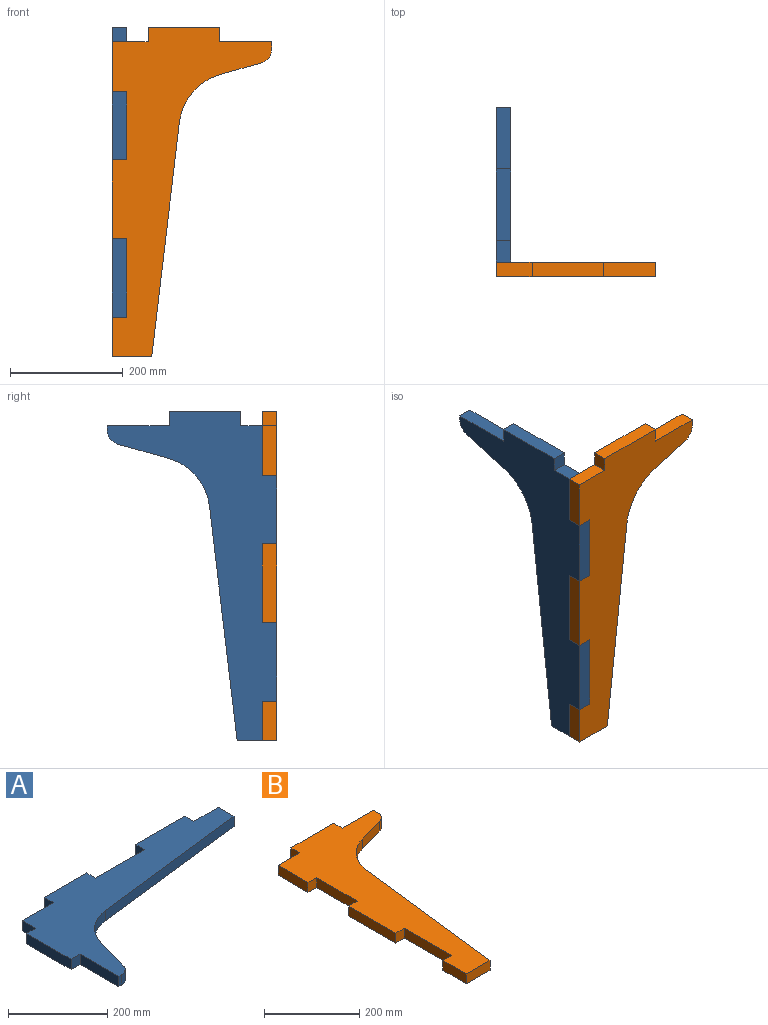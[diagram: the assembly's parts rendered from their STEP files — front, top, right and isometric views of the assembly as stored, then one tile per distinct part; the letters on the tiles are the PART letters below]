
ASSEMBLY  parts=2 mates=1
PART A: 22 faces, bbox 584.2x300.4x25.4 mm
  f0: plane 109.86x25.4mm, normal (-1,0,0), area 2790.5mm2, adj f1,f19,f20,f21
  f1: plane 25.4x8.24mm, normal (0,-1,0), area 209.4mm2, adj f0,f2,f20,f21
  f2: cylinder r=25.4mm len=25.4mm, axis (0,0,-1), area 836.7mm2, adj f1,f3,f20,f21
  f3: plane 89.39x25.4mm, normal (0.96,-0.27,0), area 2358.3mm2, adj f2,f4,f20,f21
  f4: cylinder r=101.6mm len=85.9mm, axis (0,0,-1), area 3043.6mm2, adj f3,f5,f20,f21
  f5: plane 415.09x48.99mm, normal (0.12,-0.99,0), area 10616.3mm2, adj f4,f6,f20,f21
  f6: plane 44.65x25.4mm, normal (1,0,0), area 1134mm2, adj f5,f7,f20,f21
  f7: plane 69.85x25.4mm, normal (0,1,0), area 1774.2mm2, adj f6,f8,f20,f21
  f8: plane 25.4x25.4mm, normal (1,0,0), area 645.2mm2, adj f7,f9,f20,f21
  f9: plane 139.7x25.4mm, normal (0,1,0), area 3548.4mm2, adj f8,f10,f20,f21
  f10: plane 25.4x25.4mm, normal (-1,0,0), area 645.2mm2, adj f9,f11,f20,f21
  f11: plane 139.7x25.4mm, normal (0,1,0), area 3548.4mm2, adj f10,f12,f20,f21
  f12: plane 25.4x25.4mm, normal (1,0,0), area 645.2mm2, adj f11,f13,f20,f21
  f13: plane 120.65x25.4mm, normal (0,1,0), area 3064.5mm2, adj f12,f14,f20,f21
  f14: plane 25.4x25.4mm, normal (-1,0,0), area 645.2mm2, adj f13,f15,f20,f21
  f15: plane 88.9x25.4mm, normal (0,1,0), area 2258.1mm2, adj f14,f16,f20,f21
  f16: plane 38.1x25.4mm, normal (-1,0,0), area 967.7mm2, adj f15,f17,f20,f21
  f17: plane 25.4x25.4mm, normal (0,1,0), area 645.2mm2, adj f16,f18,f20,f21
  f18: plane 127x25.4mm, normal (-1,0,0), area 3225.8mm2, adj f17,f19,f20,f21
  f19: plane 25.4x25.4mm, normal (0,-1,0), area 645.2mm2, adj f0,f18,f20,f21
  f20: plane 584.2x300.36mm, normal (0,0,1), area 62606.8mm2, adj f0,f1,f2,f3,f4,f5,f6,f7
  f21: plane 584.2x300.36mm, normal (0,0,-1), area 62606.8mm2, adj f0,f1,f2,f3,f4,f5,f6,f7
PART B: 22 faces, bbox 283x584.2x25.4 mm
  f0: plane 25.4x25.4mm, normal (0,-1,0), area 645.2mm2, adj f1,f19,f20,f21
  f1: plane 139.7x25.4mm, normal (-1,0,0), area 3548.4mm2, adj f0,f2,f20,f21
  f2: plane 25.4x25.4mm, normal (0,1,0), area 645.2mm2, adj f1,f3,f20,f21
  f3: plane 69.85x25.4mm, normal (-1,0,0), area 1774.2mm2, adj f2,f4,f20,f21
  f4: plane 70.05x25.4mm, normal (0,-1,0), area 1779.1mm2, adj f3,f5,f20,f21
  f5: plane 415.09x48.99mm, normal (0.99,-0.12,0), area 10616.3mm2, adj f4,f6,f20,f21
  f6: cylinder r=101.6mm len=85.9mm, axis (0,0,-1), area 3043.6mm2, adj f5,f7,f20,f21
  f7: plane 71.98x25.4mm, normal (0.27,-0.96,0), area 1899mm2, adj f6,f8,f20,f21
  f8: cylinder r=25.4mm len=25.4mm, axis (0,0,-1), area 836.7mm2, adj f7,f9,f20,f21
  f9: plane 25.4x13.13mm, normal (1,0,0), area 333.6mm2, adj f8,f10,f20,f21
  f10: plane 92.46x25.4mm, normal (0,1,0), area 2348.4mm2, adj f9,f11,f20,f21
  f11: plane 25.4x25.4mm, normal (1,0,0), area 645.2mm2, adj f10,f12,f20,f21
  f12: plane 127x25.4mm, normal (0,1,0), area 3225.8mm2, adj f11,f13,f20,f21
  f13: plane 25.4x25.4mm, normal (-1,0,0), area 645.2mm2, adj f12,f14,f20,f21
  f14: plane 63.5x25.4mm, normal (0,1,0), area 1612.9mm2, adj f13,f15,f20,f21
  f15: plane 88.9x25.4mm, normal (-1,0,0), area 2258.1mm2, adj f14,f16,f20,f21
  f16: plane 25.4x25.4mm, normal (0,-1,0), area 645.2mm2, adj f15,f17,f20,f21
  f17: plane 120.65x25.4mm, normal (-1,0,0), area 3064.5mm2, adj f16,f18,f20,f21
  f18: plane 25.4x25.4mm, normal (0,1,0), area 645.2mm2, adj f17,f19,f20,f21
  f19: plane 139.7x25.4mm, normal (-1,0,0), area 3548.4mm2, adj f0,f18,f20,f21
  f20: plane 584.2x282.96mm, normal (0,0,1), area 63053.5mm2, adj f0,f1,f2,f3,f4,f5,f6,f7
  f21: plane 584.2x282.96mm, normal (0,0,-1), area 63053.5mm2, adj f0,f1,f2,f3,f4,f5,f6,f7
PLACE A rot(axis=(0.71,0,-0.71),180deg) t=(-1026.59,371.08,-836.79)mm
PLACE B rot(axis=(1,0,0),90deg) t=(167.21,-211.1,-577.04)mm
MATE fastened B.f16 <-> A.f14  axis (0,0,1) through (-1039.29,-223.8,-81.74)mm
